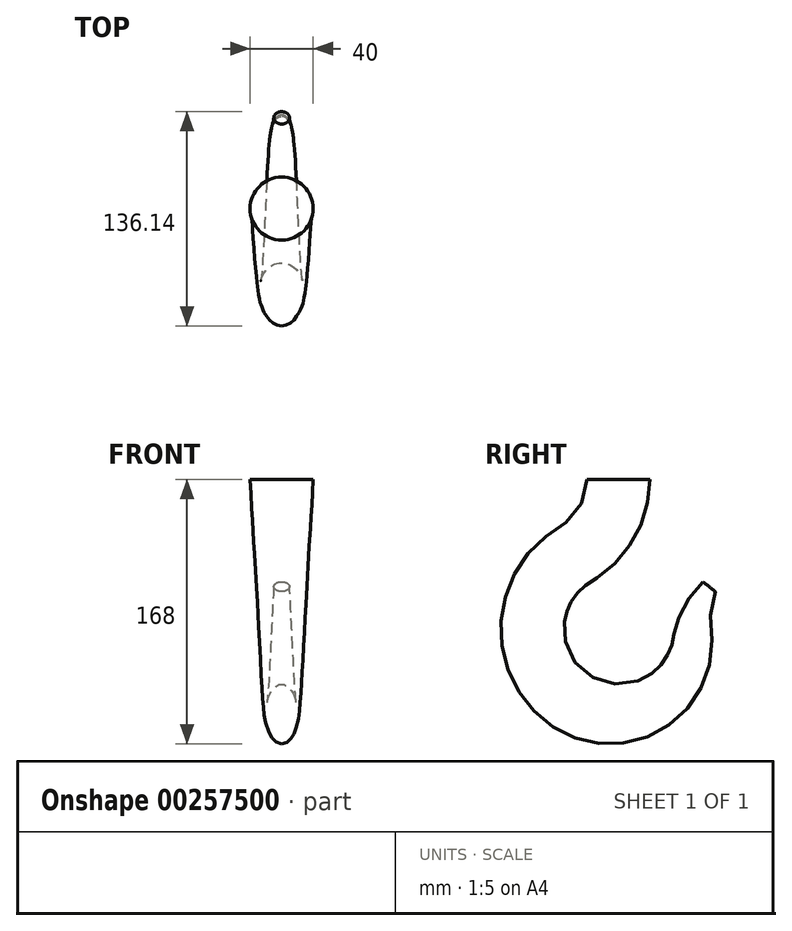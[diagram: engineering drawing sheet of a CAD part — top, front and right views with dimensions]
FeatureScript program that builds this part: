
annotation { "Feature Type Name" : "Feature", "Feature Type Description" : "" }
export const myFeature = defineFeature(function(context is Context, id is Id, definition is map)
    precondition{}
    {
        {
            var Q0;
            Q0=qCreatedBy(makeId("Right.planeOp"),FACE);
            var sketch = newSketch(context, id + "F0", { "sketchPlane" : qUnion([Q0])});
            skLineSegment(sketch, "E0", {"start": v(0, 27) * mm, "end": v(0, -168) * mm, "construction": true});
            skLineSegment(sketch, "E1", {"start": v(-68, -95) * mm, "end": v(86.28, -95) * mm, "construction": true});
            skLineSegment(sketch, "E2", {"start": v(-20.45, 0) * mm, "end": v(19.55, 0) * mm});
            skArc(sketch, "E3", {"start": v(-20.45, 0) * mm, "mid": v(-25.1, -17.43) * mm, "end": v(-37.8, -30.23) * mm});
            skArc(sketch, "E4", {"start": v(-37.8, -30.23) * mm, "mid": v(-74.88, -90.68) * mm, "end": v(-45, -155) * mm});
            skArc(sketch, "E5", {"start": v(19.55, 0) * mm, "mid": v(9.59, -37.35) * mm, "end": v(-17.64, -64.77) * mm});
            skArc(sketch, "E6", {"start": v(-17.64, -64.77) * mm, "mid": v(-19.64, -123.97) * mm, "end": v(34.61, -100.2) * mm});
            skArc(sketch, "E7", {"start": v(-45, -155) * mm, "mid": v(26.7, -159.17) * mm, "end": v(58.48, -94.76) * mm});
            skArc(sketch, "E8", {"start": v(34.61, -100.2) * mm, "mid": v(40.94, -81) * mm, "end": v(53.27, -65) * mm});
            skCircle(sketch, "E9", {"center": v(57.22, -68.07) * mm, "radius": 5 * mm, "construction": true});
            skLineSegment(sketch, "E10", {"start": v(0, -168) * mm, "end": v(-77.63, -168) * mm, "construction": true});
            skLineSegment(sketch, "E11", {"start": v(53.27, -65) * mm, "end": v(61.14, -71.17) * mm});
            skArc(sketch, "E12", {"start": v(58.48, -94.76) * mm, "mid": v(58.39, -82.8) * mm, "end": v(61.14, -71.17) * mm});
            skSolve(sketch);
        }
        {
            var Q0;
            Q0=qCreatedBy(makeId("Top.planeOp"),FACE);
            var sketch = newSketch(context, id + "F1", { "sketchPlane" : qUnion([Q0])});
            skPoint(sketch, "E13.0", {"position": v(0, -20.45) * mm});
            skPoint(sketch, "E13.1", {"position": v(0, 19.55) * mm});
            skPoint(sketch, "E14.0", {"position": v(0, -0.45) * mm});
            skCircle(sketch, "E15", {"center": v(0, -0.45) * mm, "radius": 20 * mm});
            skSolve(sketch);
        }
        {
            var Q0;
            Q0=sQuery(id+"F0.wireOp",EDGE,"E11");
            cPlane(context, id + "F2", {"entities" : qUnion([Q0]), "cplaneType" : CPlaneType.LINE_ANGLE, "offset" : 25 * mm, "angle" : 0 * degree, "width" : 150 * mm, "height" : 150 * mm});
        }
        {
            var Q0;
            Q0=qCreatedBy(id+"F2.planeOp",FACE);
            var sketch = newSketch(context, id + "F3", { "sketchPlane" : qUnion([Q0])});
            skLineSegment(sketch, "E16.0", {"start": v(0, 82.03) * mm, "end": v(0, 92.03) * mm, "construction": true});
            skCircle(sketch, "E17", {"center": v(0, 87.03) * mm, "radius": 5 * mm});
            skSolve(sketch);
        }
        {
            var Q0;
            Q0=qCreatedBy(makeId("Right.planeOp"),FACE);
            var sketch = newSketch(context, id + "F4", { "sketchPlane" : qUnion([Q0])});
            skArc(sketch, "E18.0", {"start": v(-20.45, 0) * mm, "mid": v(-25.1, -17.43) * mm, "end": v(-37.8, -30.23) * mm});
            skArc(sketch, "E18.1", {"start": v(-37.8, -30.23) * mm, "mid": v(-74.88, -90.68) * mm, "end": v(-45, -155) * mm});
            skArc(sketch, "E18.2", {"start": v(-45, -155) * mm, "mid": v(26.7, -159.17) * mm, "end": v(58.48, -94.76) * mm});
            skArc(sketch, "E18.3", {"start": v(58.48, -94.76) * mm, "mid": v(58.39, -82.8) * mm, "end": v(61.14, -71.17) * mm});
            skSolve(sketch);
        }
        {
            var Q0;
            Q0=qCreatedBy(makeId("Right.planeOp"),FACE);
            var sketch = newSketch(context, id + "F5", { "sketchPlane" : qUnion([Q0])});
            skArc(sketch, "E19.0", {"start": v(19.55, 0) * mm, "mid": v(9.59, -37.35) * mm, "end": v(-17.64, -64.77) * mm});
            skArc(sketch, "E19.1", {"start": v(-17.64, -64.77) * mm, "mid": v(-19.64, -123.97) * mm, "end": v(34.61, -100.2) * mm});
            skArc(sketch, "E19.2", {"start": v(34.61, -100.2) * mm, "mid": v(40.94, -81) * mm, "end": v(53.27, -65) * mm});
            skSolve(sketch);
        }
        {
            var Q0;
            Q0=makeQuery(id+"F1.imprint","IMPRINT",FACE,{"disambiguationData":[TD([[makeQuery(id+"F1.imprint","IMPRINT",EDGE,{"derivedFrom":sQuery(id+"F1.wireOp",EDGE,"E15")}),1.0]])]});
            var Q1;
            Q1=makeQuery(id+"F3.imprint","IMPRINT",FACE,{"disambiguationData":[TD([[makeQuery(id+"F3.imprint","IMPRINT",EDGE,{"derivedFrom":sQuery(id+"F3.wireOp",EDGE,"E17")}),1.0]])]});
            var Q2;
            Q2 = qConstructionFilter(qBodyType(qCreatedBy(id + "F4" ,EDGE), BodyType.WIRE), ConstructionObject.NO);
            var Q3;
            Q3 = qConstructionFilter(qBodyType(qCreatedBy(id + "F5" ,EDGE), BodyType.WIRE), ConstructionObject.NO);
            loft(context, id + "F6", {"addGuides" : true, "sheetProfilesArray" : [{ "sheetProfileEntities" : qUnion([Q0]) }, { "sheetProfileEntities" : qUnion([Q1]) }], "guidesArray" : [{ "guideEntities" : qUnion([Q2]), "guideDerivativeType" : LoftGuideDerivativeType.DEFAULT, "guideDerivativeMagnitude" : 1 }, { "guideEntities" : qUnion([Q3]), "guideDerivativeType" : LoftGuideDerivativeType.DEFAULT, "guideDerivativeMagnitude" : 1 }]});
        }
    });
